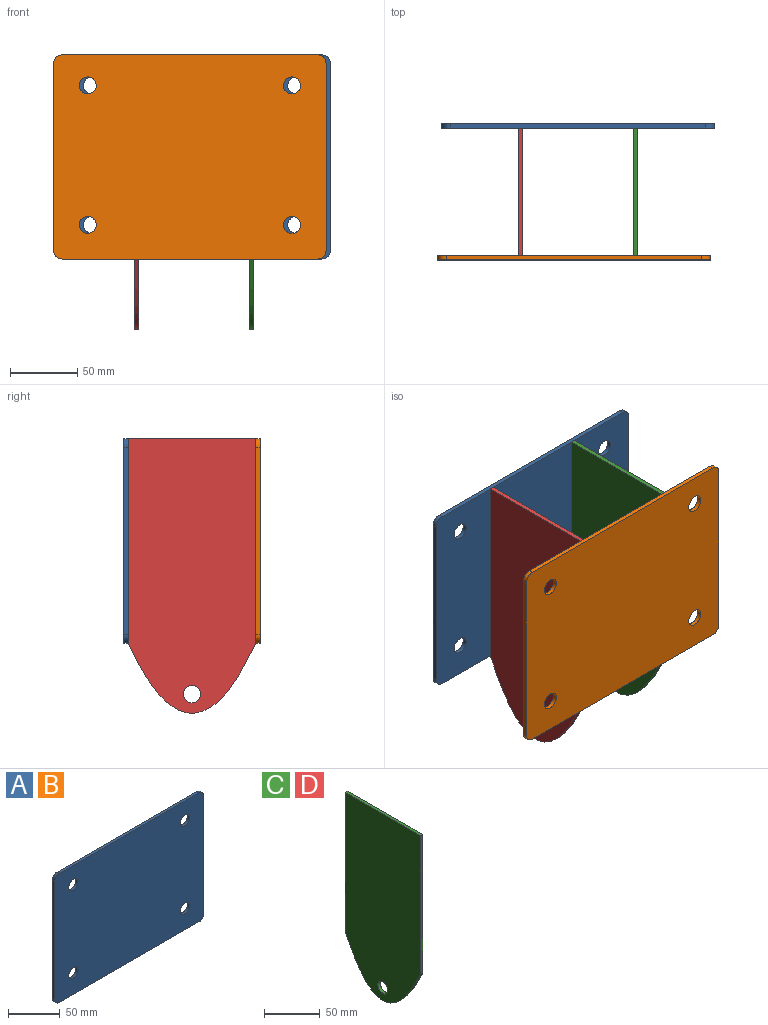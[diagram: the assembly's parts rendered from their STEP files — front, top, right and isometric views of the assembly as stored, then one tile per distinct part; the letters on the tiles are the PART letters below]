
ASSEMBLY  parts=4 mates=3
PART A: 14 faces, bbox 203.2x3.2x152.4 mm
  f0: plane 139.7x3.18mm, normal (-1,0,0), area 443.5mm2, adj f1,f11,f12,f13
  f1: cylinder r=6.35mm len=6.35mm, axis (0,1,0), area 31.7mm2, adj f0,f2,f12,f13
  f2: plane 190.5x3.18mm, normal (0,0,-1), area 604.8mm2, adj f1,f3,f12,f13
  f3: cylinder r=6.35mm len=6.35mm, axis (0,1,0), area 31.7mm2, adj f2,f4,f12,f13
  f4: plane 139.7x3.18mm, normal (1,0,0), area 443.5mm2, adj f3,f5,f12,f13
  f5: cylinder r=6.35mm len=6.35mm, axis (0,1,0), area 31.7mm2, adj f4,f6,f12,f13
  f6: plane 190.5x3.18mm, normal (0,0,1), area 604.8mm2, adj f5,f11,f12,f13
  f7: cylinder r=6.35mm len=12.7mm, axis (0,1,0), area 126.7mm2, adj f12,f13
  f8: cylinder r=6.35mm len=12.7mm, axis (0,1,0), area 126.7mm2, adj f12,f13
  f9: cylinder r=6.35mm len=12.7mm, axis (0,1,0), area 126.7mm2, adj f12,f13
  f10: cylinder r=6.35mm len=12.7mm, axis (0,1,0), area 126.7mm2, adj f12,f13
  f11: cylinder r=6.35mm len=6.35mm, axis (0,1,0), area 31.7mm2, adj f0,f6,f12,f13
  f12: plane 203.2x152.4mm, normal (0,-1,0), area 30426.4mm2, adj f0,f1,f2,f3,f4,f5,f6,f7
  f13: plane 203.2x152.4mm, normal (0,1,0), area 30426.4mm2, adj f0,f1,f2,f3,f4,f5,f6,f7
PART B: same geometry as A
PART C: 7 faces, bbox 3.2x95.3x224.4 mm
  f0: plane 152.4x3.18mm, normal (0,-1,0), area 483.9mm2, adj f1,f3,f5,f6
  f1: extruded ~95.25x52.34mm, area 470.3mm2, adj f0,f2,f5,f6
  f2: plane 152.4x3.18mm, normal (0,1,0), area 483.9mm2, adj f1,f3,f5,f6
  f3: plane 95.25x3.18mm, normal (0,0,1), area 302.4mm2, adj f0,f2,f5,f6
  f4: cylinder r=6.35mm len=12.7mm, axis (-1,0,0), area 126.7mm2, adj f5,f6
  f5: plane 224.37x95.25mm, normal (1,0,0), area 17713.2mm2, adj f0,f1,f2,f3,f4
  f6: plane 224.37x95.25mm, normal (-1,0,0), area 17713.2mm2, adj f0,f1,f2,f3,f4
PART D: same geometry as C
PLACE A rot(axis=(0,0,1),180deg) t=(-28.97,-9.02,36.08)mm
PLACE B t=(-94.56,-104.27,36.08)mm
PLACE C t=(-18.9,-9.86,-16.32)mm
PLACE D t=(-104.62,-9.86,-16.32)mm
MATE fastened B.f6 <-> C.f3  axis (0,0,-1) through (-18.9,-104.27,123.59)mm
MATE fastened D.f3 <-> A.f6  axis (0,0,-1) through (-104.62,-9.02,123.59)mm
MATE fastened A.f6 <-> C.f3  axis (0,0,-1) through (-15.72,-9.02,123.59)mm
